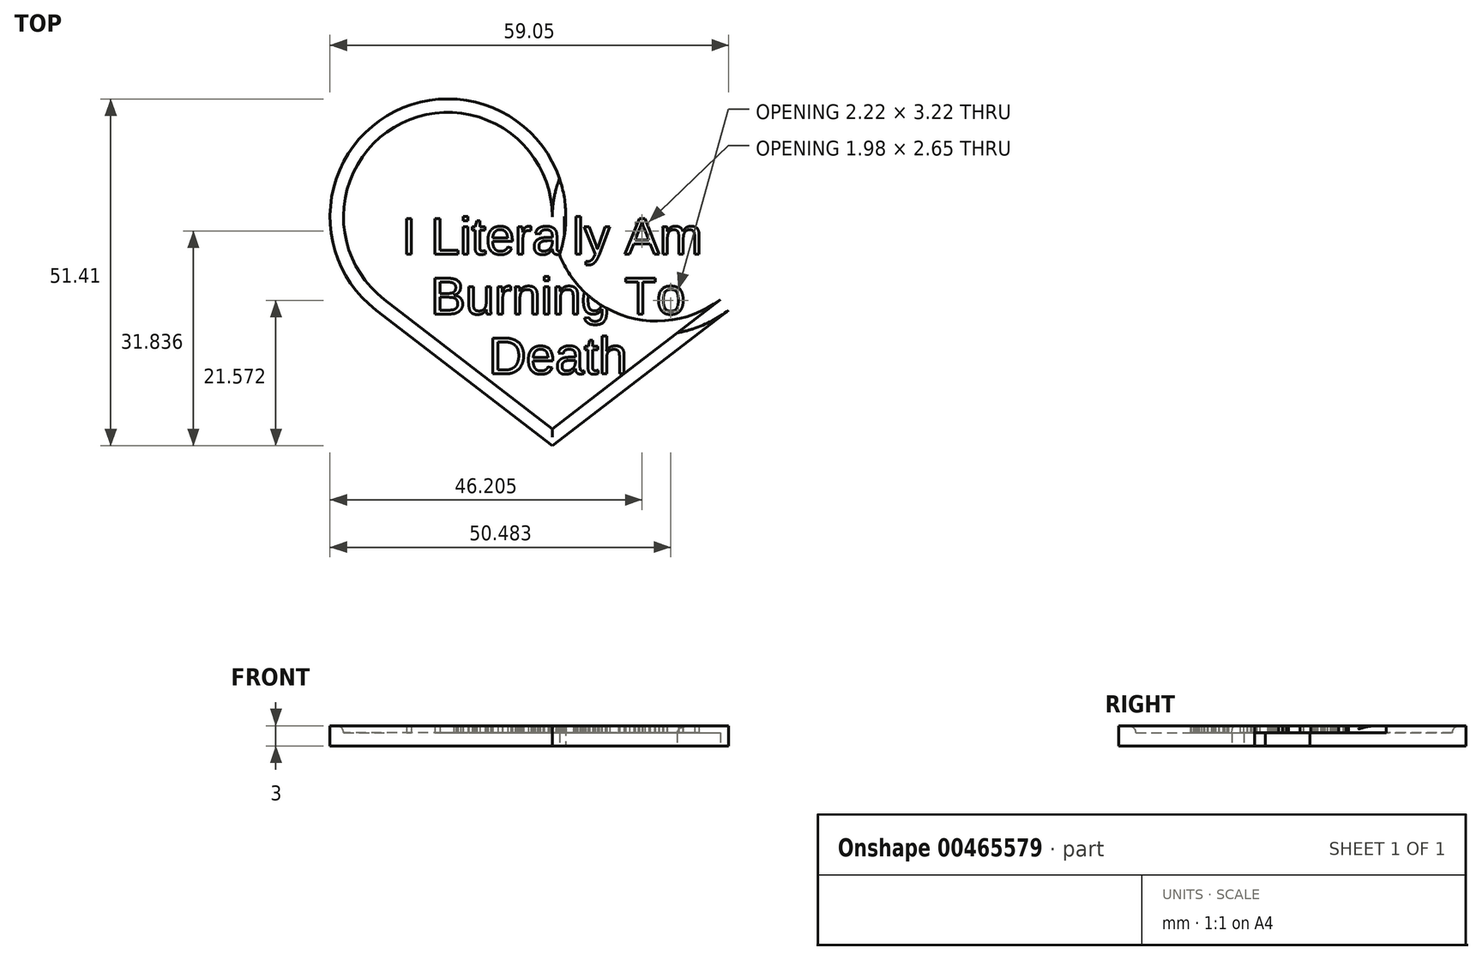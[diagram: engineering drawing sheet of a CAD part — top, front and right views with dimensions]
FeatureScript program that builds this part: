
annotation { "Feature Type Name" : "Feature", "Feature Type Description" : "" }
export const myFeature = defineFeature(function(context is Context, id is Id, definition is map)
    precondition{}
    {
        {
            var Q0;
            Q0=qCreatedBy(makeId("Top.planeOp"),FACE);
            var sketch = newSketch(context, id + "F0", { "sketchPlane" : qUnion([Q0])});
            skArc(sketch, "E0", {"start": v(30.93, 0) * mm, "mid": v(15.46, 15.46) * mm, "end": v(0, 0) * mm});
            skArc(sketch, "E1", {"start": v(0, 0) * mm, "mid": v(-15.46, 15.46) * mm, "end": v(-30.93, 0) * mm});
            skArc(sketch, "E2", {"start": v(-30.93, 0) * mm, "mid": v(-15.46, -15.46) * mm, "end": v(0, 0) * mm});
            skArc(sketch, "E3", {"start": v(0, 0) * mm, "mid": v(15.46, 15.46) * mm, "end": v(30.93, 0) * mm});
            skArc(sketch, "E4", {"start": v(0, 0) * mm, "mid": v(15.46, -15.46) * mm, "end": v(30.93, 0) * mm});
            skLineSegment(sketch, "E5", {"start": v(0, -31.43) * mm, "end": v(-24.9, -12.25) * mm});
            skLineSegment(sketch, "E6", {"start": v(0, -31.43) * mm, "end": v(24.9, -12.25) * mm});
            skArc(sketch, "E7.0", {"start": v(2, 0) * mm, "mid": v(-15.46, 17.46) * mm, "end": v(-32.93, 0) * mm});
            skArc(sketch, "E7.1", {"start": v(-32.93, 0) * mm, "mid": v(-15.46, -17.46) * mm, "end": v(2, 0) * mm});
            skArc(sketch, "E8.0", {"start": v(-2, 0) * mm, "mid": v(15.46, -17.46) * mm, "end": v(32.93, 0) * mm});
            skArc(sketch, "E8.1", {"start": v(-2, 0) * mm, "mid": v(15.46, 17.46) * mm, "end": v(32.93, 0) * mm});
            skLineSegment(sketch, "E9.0", {"start": v(0, -33.95) * mm, "end": v(-26.12, -13.84) * mm});
            skLineSegment(sketch, "E9.1", {"start": v(0, -33.95) * mm, "end": v(26.12, -13.84) * mm});
            skSolve(sketch);
        }
        {
            var Q0;
            {var subQ0=sQuery(id+"F0.wireOp",EDGE,"E2");var subQ6=sQuery(id+"F0.wireOp",EDGE,"E1");var subQ7=makeQuery(id+"F0.imprint","INTERSECT",VERTEX,{"derivedFrom":[subQ6,subQ0]});Q0=makeQuery(id+"F0.imprint","IMPRINT",FACE,{"disambiguationData":[TD([[makeQuery(id+"F0.imprint","IMPRINT",EDGE,{"disambiguationData":[TD([[subQ7,1.0]])],"derivedFrom":subQ6}),1.0]])]});}
            var Q1;
            {var subQ3=sQuery(id+"F0.wireOp",EDGE,"E8.1");var subQ5=sQuery(id+"F0.wireOp",EDGE,"E8.0");var subQ7=makeQuery(id+"F0.imprint","INTERSECT",VERTEX,{"disambiguationData":[OD(0.0)],"derivedFrom":[subQ5,subQ3]});Q1=makeQuery(id+"F0.imprint","IMPRINT",FACE,{"disambiguationData":[TD([[makeQuery(id+"F0.imprint","IMPRINT",EDGE,{"disambiguationData":[TD([[subQ7,-1.0]])],"derivedFrom":subQ5}),1.0]])]});}
            var Q2;
            {var subQ0=sQuery(id+"F0.wireOp",EDGE,"E4");var subQ5=sQuery(id+"F0.wireOp",EDGE,"E7.1");var subQ6=makeQuery(id+"F0.imprint","INTERSECT",VERTEX,{"derivedFrom":[subQ0,subQ5]});Q2=makeQuery(id+"F0.imprint","IMPRINT",FACE,{"disambiguationData":[TD([[makeQuery(id+"F0.imprint","IMPRINT",EDGE,{"disambiguationData":[TD([[subQ6,1.0]])],"derivedFrom":subQ5}),1.0]])]});}
            var Q3;
            {var subQ0=sQuery(id+"F0.wireOp",EDGE,"E5");var subQ1=sQuery(id+"F0.wireOp",EDGE,"E2");var subQ2=makeQuery(id+"F0.imprint","INTERSECT",VERTEX,{"derivedFrom":[subQ1,subQ0]});Q3=makeQuery(id+"F0.imprint","IMPRINT",FACE,{"disambiguationData":[TD([[makeQuery(id+"F0.imprint","IMPRINT",EDGE,{"disambiguationData":[TD([[subQ2,-1.0]])],"derivedFrom":subQ1}),-1.0]])]});}
            var Q4;
            {var subQ0=sQuery(id+"F0.wireOp",EDGE,"E6");var subQ1=sQuery(id+"F0.wireOp",EDGE,"E4");var subQ2=makeQuery(id+"F0.imprint","INTERSECT",VERTEX,{"derivedFrom":[subQ1,subQ0]});Q4=makeQuery(id+"F0.imprint","IMPRINT",FACE,{"disambiguationData":[TD([[makeQuery(id+"F0.imprint","IMPRINT",EDGE,{"disambiguationData":[TD([[subQ2,1.0]])],"derivedFrom":subQ1}),-1.0]])]});}
            var Q5;
            {var subQ3=sQuery(id+"F0.wireOp",EDGE,"E7.0");var subQ5=sQuery(id+"F0.wireOp",EDGE,"E7.1");var subQ7=makeQuery(id+"F0.imprint","INTERSECT",VERTEX,{"disambiguationData":[OD(0.0)],"derivedFrom":[subQ3,subQ5]});Q5=makeQuery(id+"F0.imprint","IMPRINT",FACE,{"disambiguationData":[TD([[makeQuery(id+"F0.imprint","IMPRINT",EDGE,{"disambiguationData":[TD([[subQ7,-1.0]])],"derivedFrom":subQ3}),1.0]])]});}
            var Q6;
            {var subQ3=sQuery(id+"F0.wireOp",EDGE,"E3");var subQ5=sQuery(id+"F0.wireOp",EDGE,"E4");var subQ6=makeQuery(id+"F0.imprint","INTERSECT",VERTEX,{"derivedFrom":[subQ3,subQ5]});Q6=makeQuery(id+"F0.imprint","IMPRINT",FACE,{"disambiguationData":[TD([[makeQuery(id+"F0.imprint","IMPRINT",EDGE,{"disambiguationData":[TD([[subQ6,1.0]])],"derivedFrom":subQ3}),-1.0]])]});}
            var Q7;
            {var subQ0=sQuery(id+"F0.wireOp",EDGE,"E6");var subQ1=sQuery(id+"F0.wireOp",EDGE,"E5");var subQ2=makeQuery(id+"F0.imprint","INTERSECT",VERTEX,{"derivedFrom":[subQ1,subQ0]});Q7=makeQuery(id+"F0.imprint","IMPRINT",FACE,{"disambiguationData":[TD([[makeQuery(id+"F0.imprint","IMPRINT",EDGE,{"disambiguationData":[TD([[subQ2,-1.0]])],"derivedFrom":subQ1}),-1.0]])]});}
            extrude(context, id + "F1", {"entities" : qUnion([Q0, Q1, Q2, Q3, Q4, Q5, Q6, Q7]), "depth" : 2 * mm});
        }
        {
            var Q0;
            {var subQ0=sQuery(id+"F0.wireOp",EDGE,"E2");var subQ1=sQuery(id+"F0.wireOp",EDGE,"E1");var subQ2=makeQuery(id+"F0.imprint","INTERSECT",VERTEX,{"derivedFrom":[subQ1,subQ0]});Q0=makeQuery(id+"F0.imprint","IMPRINT",FACE,{"disambiguationData":[TD([[makeQuery(id+"F0.imprint","IMPRINT",EDGE,{"disambiguationData":[TD([[subQ2,1.0]])],"derivedFrom":subQ1}),-1.0]])]});}
            var Q1;
            {var subQ3=sQuery(id+"F0.wireOp",EDGE,"E3");var subQ9=sQuery(id+"F0.wireOp",EDGE,"E4");var subQ12=makeQuery(id+"F0.imprint","INTERSECT",VERTEX,{"derivedFrom":[subQ3,subQ9]});Q1=makeQuery(id+"F0.imprint","IMPRINT",FACE,{"disambiguationData":[TD([[makeQuery(id+"F0.imprint","IMPRINT",EDGE,{"disambiguationData":[TD([[subQ12,1.0]])],"derivedFrom":subQ3}),1.0]])]});}
            var Q2;
            {var subQ3=sQuery(id+"F0.wireOp",EDGE,"E8.1");var subQ5=sQuery(id+"F0.wireOp",EDGE,"E7.0");var subQ7=makeQuery(id+"F0.imprint","INTERSECT",VERTEX,{"derivedFrom":[subQ5,subQ3]});Q2=makeQuery(id+"F0.imprint","IMPRINT",FACE,{"disambiguationData":[TD([[makeQuery(id+"F0.imprint","IMPRINT",EDGE,{"disambiguationData":[TD([[subQ7,1.0]])],"derivedFrom":subQ5}),1.0]])]});}
            var Q3;
            {var subQ0=sQuery(id+"F0.wireOp",EDGE,"E9.0");Q3=makeQuery(id+"F0.imprint","IMPRINT",FACE,{"disambiguationData":[TD([[makeQuery(id+"F0.imprint","IMPRINT",EDGE,{"derivedFrom":subQ0}),-1.0]])]});}
            extrude(context, id + "F2", {"entities" : qUnion([Q0, Q1, Q2, Q3]), "operationType" : NewBodyOperationType.ADD, "depth" : 3 * mm});
        }
        {
            var Q0;
            Q0=makeQuery(id+"F2.opExtrude","CAP_EDGE",EDGE,{"disambiguationData":[OSD([sQuery(id+"F0.wireOp",EDGE,"E1"),sQuery(id+"F0.wireOp",EDGE,"E2")])],"isStart":false});
            var Q1;
            Q1=makeQuery(id+"F2.opExtrude","CAP_EDGE",EDGE,{"disambiguationData":[OSD([sQuery(id+"F0.wireOp",EDGE,"E6")])],"isStart":false});
            var Q2;
            Q2=makeQuery(id+"F2.opExtrude","CAP_EDGE",EDGE,{"disambiguationData":[OSD([sQuery(id+"F0.wireOp",EDGE,"E5")])],"isStart":false});
            var Q3;
            Q3=makeQuery(id+"F2.opExtrude","CAP_EDGE",EDGE,{"disambiguationData":[OSD([sQuery(id+"F0.wireOp",EDGE,"E3"),sQuery(id+"F0.wireOp",EDGE,"E4")])],"isStart":false});
            fillet(context, id + "F3", {"entities" : qUnion([Q0, Q1, Q2, Q3]), "radius" : 1 * mm, "tangentPropagation" : true, "allowEdgeOverflow" : false});
        }
        {
            var Q0;
            Q0=makeQuery(id+"F1.opExtrude","CAP_FACE",FACE,{"disambiguationData":[OSD([sQuery(id+"F0.wireOp",EDGE,"E1"),sQuery(id+"F0.wireOp",EDGE,"E2"),sQuery(id+"F0.wireOp",EDGE,"E3"),sQuery(id+"F0.wireOp",EDGE,"E4"),sQuery(id+"F0.wireOp",EDGE,"E5"),sQuery(id+"F0.wireOp",EDGE,"E6")])],"isStart":false});
            var sketch = newSketch(context, id + "F4", { "sketchPlane" : qUnion([Q0])});
            skText(sketch, "E10", { "text": "I Literally Am\n  Burning To\n      Death", "fontName": "Arimo-Regular.ttf"});
            skPoint(sketch, "E10.firstSnap0", {"position": v(-22.29, 13.87) * mm});
            skPoint(sketch, "E10.secondSnap0", {"position": v(22.29, 13.87) * mm});
            const initialGuessF4  = {"E10": [-0.02229, -0.00555, 1, 0, 0.00555]};
            skSetInitialGuess(sketch, initialGuessF4);
            skSolve(sketch);
        }
        {
            var Q0;
            Q0=makeQuery(id+"F4.imprint","IMPRINT",FACE,{"disambiguationData":[TD([[makeQuery(id+"F4.imprint","IMPRINT",EDGE,{"derivedFrom":sQuery(id+"F4.wireOp",EDGE,"E10.sketch_text.stroke-175")}),-1.0]])]});
            var Q1;
            Q1=makeQuery(id+"F4.imprint","IMPRINT",FACE,{"disambiguationData":[TD([[makeQuery(id+"F4.imprint","IMPRINT",EDGE,{"derivedFrom":sQuery(id+"F4.wireOp",EDGE,"E10.sketch_text.stroke-198")}),-1.0]])]});
            var Q2;
            Q2=makeQuery(id+"F4.imprint","IMPRINT",FACE,{"disambiguationData":[TD([[makeQuery(id+"F4.imprint","IMPRINT",EDGE,{"derivedFrom":sQuery(id+"F4.wireOp",EDGE,"E10.sketch_text.stroke-219")}),-1.0]])]});
            var Q3;
            Q3=makeQuery(id+"F4.imprint","IMPRINT",FACE,{"disambiguationData":[TD([[makeQuery(id+"F4.imprint","IMPRINT",EDGE,{"derivedFrom":sQuery(id+"F4.wireOp",EDGE,"E10.sketch_text.stroke-233")}),-1.0]])]});
            var Q4;
            Q4=makeQuery(id+"F4.imprint","IMPRINT",FACE,{"disambiguationData":[TD([[makeQuery(id+"F4.imprint","IMPRINT",EDGE,{"derivedFrom":sQuery(id+"F4.wireOp",EDGE,"E10.sketch_text.stroke-258")}),-1.0]])]});
            var Q5;
            Q5=makeQuery(id+"F4.imprint","IMPRINT",FACE,{"disambiguationData":[TD([[makeQuery(id+"F4.imprint","IMPRINT",EDGE,{"derivedFrom":sQuery(id+"F4.wireOp",EDGE,"E10.sketch_text.stroke-262")}),-1.0]])]});
            var Q6;
            Q6=makeQuery(id+"F4.imprint","IMPRINT",FACE,{"disambiguationData":[TD([[makeQuery(id+"F4.imprint","IMPRINT",EDGE,{"derivedFrom":sQuery(id+"F4.wireOp",EDGE,"E10.sketch_text.stroke-254")}),-1.0]])]});
            var Q7;
            Q7=makeQuery(id+"F4.imprint","IMPRINT",FACE,{"disambiguationData":[TD([[makeQuery(id+"F4.imprint","IMPRINT",EDGE,{"derivedFrom":sQuery(id+"F4.wireOp",EDGE,"E10.sketch_text.stroke-283")}),-1.0]])]});
            var Q8;
            Q8=makeQuery(id+"F4.imprint","IMPRINT",FACE,{"disambiguationData":[TD([[makeQuery(id+"F4.imprint","IMPRINT",EDGE,{"derivedFrom":sQuery(id+"F4.wireOp",EDGE,"E10.sketch_text.stroke-316")}),-1.0]])]});
            var Q9;
            Q9=makeQuery(id+"F4.imprint","IMPRINT",FACE,{"disambiguationData":[TD([[makeQuery(id+"F4.imprint","IMPRINT",EDGE,{"derivedFrom":sQuery(id+"F4.wireOp",EDGE,"E10.sketch_text.stroke-324")}),-1.0]])]});
            var Q10;
            Q10=makeQuery(id+"F4.imprint","IMPRINT",FACE,{"disambiguationData":[TD([[makeQuery(id+"F4.imprint","IMPRINT",EDGE,{"derivedFrom":sQuery(id+"F4.wireOp",EDGE,"E10.sketch_text.stroke-425")}),-1.0]])]});
            var Q11;
            Q11=makeQuery(id+"F4.imprint","IMPRINT",FACE,{"disambiguationData":[TD([[makeQuery(id+"F4.imprint","IMPRINT",EDGE,{"derivedFrom":sQuery(id+"F4.wireOp",EDGE,"E10.sketch_text.stroke-408")}),-1.0]])]});
            var Q12;
            Q12=makeQuery(id+"F4.imprint","IMPRINT",FACE,{"disambiguationData":[TD([[makeQuery(id+"F4.imprint","IMPRINT",EDGE,{"derivedFrom":sQuery(id+"F4.wireOp",EDGE,"E10.sketch_text.stroke-355")}),-1.0]])]});
            var Q13;
            Q13=makeQuery(id+"F4.imprint","IMPRINT",FACE,{"disambiguationData":[TD([[makeQuery(id+"F4.imprint","IMPRINT",EDGE,{"derivedFrom":sQuery(id+"F4.wireOp",EDGE,"E10.sketch_text.stroke-339")}),-1.0]])]});
            var Q14;
            Q14=makeQuery(id+"F4.imprint","IMPRINT",FACE,{"disambiguationData":[TD([[makeQuery(id+"F4.imprint","IMPRINT",EDGE,{"derivedFrom":sQuery(id+"F4.wireOp",EDGE,"E10.sketch_text.stroke-14")}),-1.0]])]});
            var Q15;
            Q15=makeQuery(id+"F4.imprint","IMPRINT",FACE,{"disambiguationData":[TD([[makeQuery(id+"F4.imprint","IMPRINT",EDGE,{"derivedFrom":sQuery(id+"F4.wireOp",EDGE,"E10.sketch_text.stroke-10")}),-1.0]])]});
            var Q16;
            Q16=makeQuery(id+"F4.imprint","IMPRINT",FACE,{"disambiguationData":[TD([[makeQuery(id+"F4.imprint","IMPRINT",EDGE,{"derivedFrom":sQuery(id+"F4.wireOp",EDGE,"E10.sketch_text.stroke-4")}),-1.0]])]});
            var Q17;
            Q17=makeQuery(id+"F4.imprint","IMPRINT",FACE,{"disambiguationData":[TD([[makeQuery(id+"F4.imprint","IMPRINT",EDGE,{"derivedFrom":sQuery(id+"F4.wireOp",EDGE,"E10.sketch_text.stroke-0")}),-1.0]])]});
            var Q18;
            Q18=makeQuery(id+"F4.imprint","IMPRINT",FACE,{"disambiguationData":[TD([[makeQuery(id+"F4.imprint","IMPRINT",EDGE,{"derivedFrom":sQuery(id+"F4.wireOp",EDGE,"E10.sketch_text.stroke-18")}),-1.0]])]});
            var Q19;
            Q19=makeQuery(id+"F4.imprint","IMPRINT",FACE,{"disambiguationData":[TD([[makeQuery(id+"F4.imprint","IMPRINT",EDGE,{"derivedFrom":sQuery(id+"F4.wireOp",EDGE,"E10.sketch_text.stroke-35")}),-1.0]])]});
            var Q20;
            Q20=makeQuery(id+"F4.imprint","IMPRINT",FACE,{"disambiguationData":[TD([[makeQuery(id+"F4.imprint","IMPRINT",EDGE,{"derivedFrom":sQuery(id+"F4.wireOp",EDGE,"E10.sketch_text.stroke-53")}),-1.0]])]});
            var Q21;
            Q21=makeQuery(id+"F4.imprint","IMPRINT",FACE,{"disambiguationData":[TD([[makeQuery(id+"F4.imprint","IMPRINT",EDGE,{"derivedFrom":sQuery(id+"F4.wireOp",EDGE,"E10.sketch_text.stroke-67")}),-1.0]])]});
            var Q22;
            Q22=makeQuery(id+"F4.imprint","IMPRINT",FACE,{"disambiguationData":[TD([[makeQuery(id+"F4.imprint","IMPRINT",EDGE,{"derivedFrom":sQuery(id+"F4.wireOp",EDGE,"E10.sketch_text.stroke-106")}),-1.0]])]});
            var Q23;
            Q23=makeQuery(id+"F4.imprint","IMPRINT",FACE,{"disambiguationData":[TD([[makeQuery(id+"F4.imprint","IMPRINT",EDGE,{"derivedFrom":sQuery(id+"F4.wireOp",EDGE,"E10.sketch_text.stroke-110")}),-1.0]])]});
            var Q24;
            Q24=makeQuery(id+"F4.imprint","IMPRINT",FACE,{"disambiguationData":[TD([[makeQuery(id+"F4.imprint","IMPRINT",EDGE,{"derivedFrom":sQuery(id+"F4.wireOp",EDGE,"E10.sketch_text.stroke-143")}),-1.0]])]});
            var Q25;
            Q25=makeQuery(id+"F4.imprint","IMPRINT",FACE,{"disambiguationData":[TD([[makeQuery(id+"F4.imprint","IMPRINT",EDGE,{"derivedFrom":sQuery(id+"F4.wireOp",EDGE,"E10.sketch_text.stroke-373")}),-1.0]])]});
            var Q26;
            Q26=makeQuery(id+"F4.imprint","IMPRINT",FACE,{"disambiguationData":[TD([[makeQuery(id+"F4.imprint","IMPRINT",EDGE,{"derivedFrom":sQuery(id+"F4.wireOp",EDGE,"E10.sketch_text.stroke-128")}),-1.0]])]});
            var Q27;
            Q27=makeQuery(id+"F4.imprint","IMPRINT",FACE,{"disambiguationData":[TD([[makeQuery(id+"F4.imprint","IMPRINT",EDGE,{"derivedFrom":sQuery(id+"F4.wireOp",EDGE,"E10.sketch_text.stroke-102")}),-1.0]])]});
            extrude(context, id + "F5", {"entities" : qUnion([Q0, Q1, Q2, Q3, Q4, Q5, Q6, Q7, Q8, Q9, Q10, Q11, Q12, Q13, Q14, Q15, Q16, Q17, Q18, Q19, Q20, Q21, Q22, Q23, Q24, Q25, Q26, Q27]), "operationType" : NewBodyOperationType.ADD, "depth" : 1 * mm});
        }
    });
